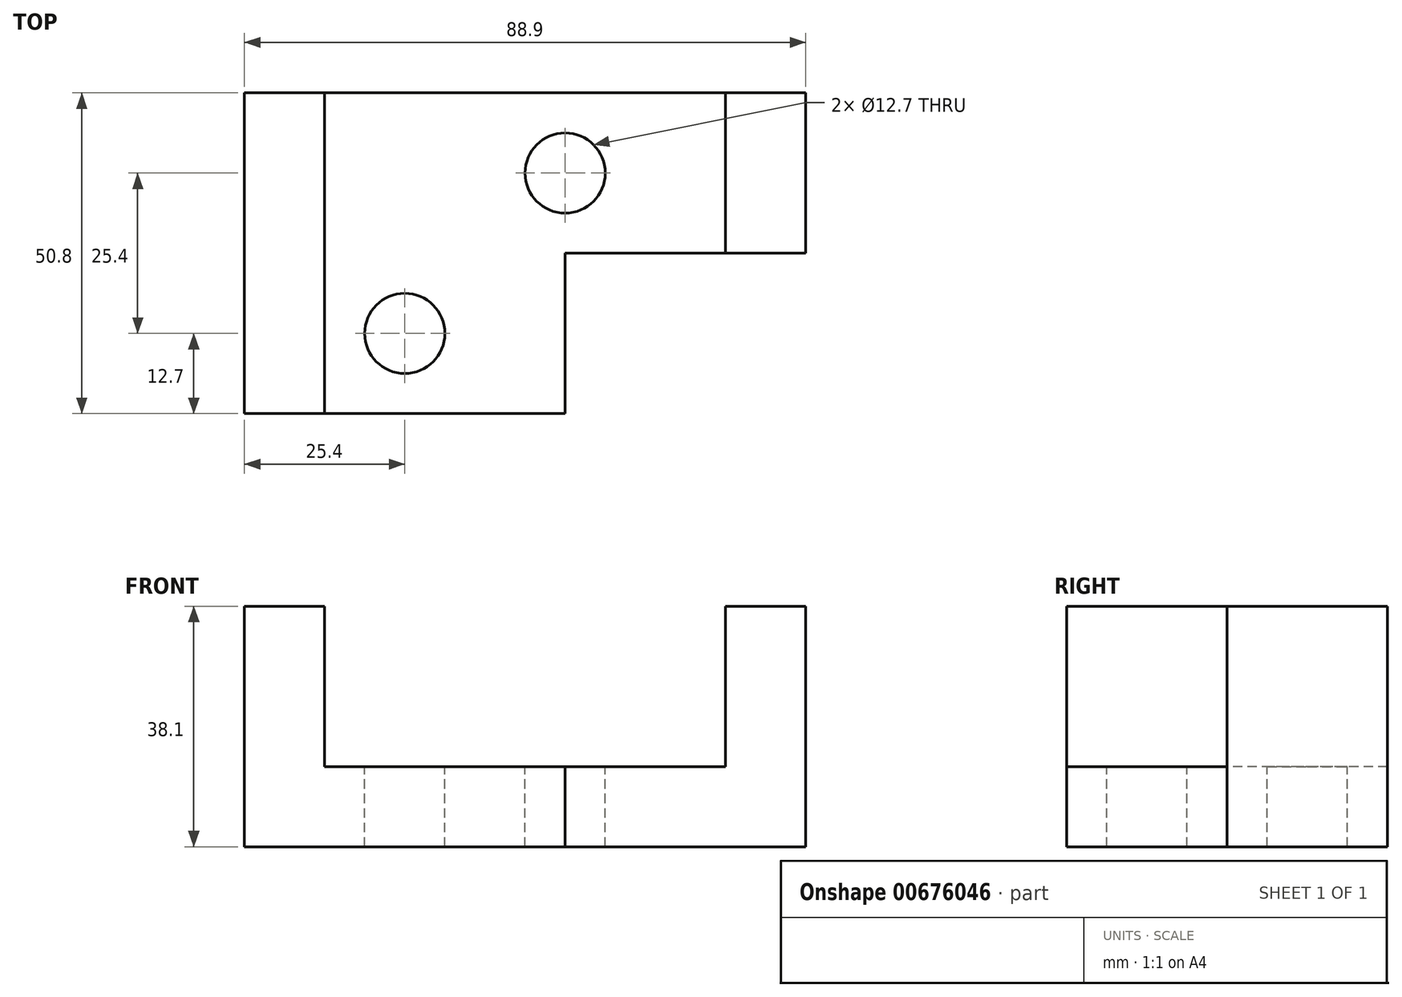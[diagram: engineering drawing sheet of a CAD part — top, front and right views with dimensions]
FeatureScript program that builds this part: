
annotation { "Feature Type Name" : "Feature", "Feature Type Description" : "" }
export const myFeature = defineFeature(function(context is Context, id is Id, definition is map)
    precondition{}
    {
        {
            var Q0;
            Q0=qCreatedBy(makeId("Front.planeOp"),FACE);
            var sketch = newSketch(context, id + "F0", { "sketchPlane" : qUnion([Q0])});
            skLineSegment(sketch, "E0.bottom", {"start": v(-44.45, 19.05) * mm, "end": v(44.45, 19.05) * mm});
            skLineSegment(sketch, "E0.top", {"start": v(-44.45, -19.05) * mm, "end": v(44.45, -19.05) * mm});
            skLineSegment(sketch, "E0.left", {"start": v(-44.45, 19.05) * mm, "end": v(-44.45, -19.05) * mm});
            skLineSegment(sketch, "E0.right", {"start": v(44.45, 19.05) * mm, "end": v(44.45, -19.05) * mm});
            skPoint(sketch, "E0.middle", {"position": v(0, 0) * mm});
            skPoint(sketch, "E1.middle", {"position": v(0, 19.05) * mm});
            skSolve(sketch);
        }
        {
            var Q0;
            Q0 = qSketchRegion(id + "F0", true);
            extrude(context, id + "F1", {"entities" : qUnion([Q0]), "depth" : 50.8 * mm, "offsetDistance" : 25.4 * mm});
        }
        {
            var Q0;
            Q0=makeQuery(id+"F1.opExtrude","CAP_FACE",FACE,{"disambiguationData":[OSD([sQuery(id+"F0.wireOp",EDGE,"E0.bottom"),sQuery(id+"F0.wireOp",EDGE,"E0.top"),sQuery(id+"F0.wireOp",EDGE,"E0.left"),sQuery(id+"F0.wireOp",EDGE,"E0.right")])],"isStart":false});
            var sketch = newSketch(context, id + "F2", { "sketchPlane" : qUnion([Q0])});
            skLineSegment(sketch, "E2.bottom", {"start": v(-31.75, 19.05) * mm, "end": v(31.75, 19.05) * mm});
            skLineSegment(sketch, "E2.top", {"start": v(-31.75, -6.35) * mm, "end": v(31.75, -6.35) * mm});
            skLineSegment(sketch, "E2.left", {"start": v(-31.75, 19.05) * mm, "end": v(-31.75, -6.35) * mm});
            skLineSegment(sketch, "E2.right", {"start": v(31.75, 19.05) * mm, "end": v(31.75, -6.35) * mm});
            skPoint(sketch, "E2.middle", {"position": v(0, 6.35) * mm});
            skSolve(sketch);
        }
        {
            var Q0;
            Q0 = qSketchRegion(id + "F2", true);
            extrude(context, id + "F3", {"entities" : qUnion([Q0]), "operationType" : NewBodyOperationType.REMOVE, "endBound" : BoundingType.THROUGH_ALL, "oppositeDirection" : true, "depth" : 25.4 * mm, "offsetDistance" : 25.4 * mm});
        }
        {
            var Q0;
            {var subQ0=sQuery(id+"F0.wireOp",EDGE,"E0.right");var subQ3=sQuery(id+"F0.wireOp",EDGE,"E0.bottom");Q0=makeQuery(id+"F3.boolean.opBoolean","SPLIT",FACE,{"disambiguationData":[TD([makeQuery(id+"F1.opExtrude","SWEPT_FACE",FACE,{"disambiguationData":[OSD([subQ0])]})])],"derivedFrom":makeQuery(id+"F1.opExtrude","SWEPT_FACE",FACE,{"disambiguationData":[OSD([subQ3])]})});}
            var sketch = newSketch(context, id + "F4", { "sketchPlane" : qUnion([Q0])});
            skLineSegment(sketch, "E3.bottom", {"start": v(44.45, -50.8) * mm, "end": v(6.35, -50.8) * mm});
            skLineSegment(sketch, "E3.top", {"start": v(44.45, -25.4) * mm, "end": v(6.35, -25.4) * mm});
            skLineSegment(sketch, "E3.left", {"start": v(44.45, -50.8) * mm, "end": v(44.45, -25.4) * mm});
            skLineSegment(sketch, "E3.right", {"start": v(6.35, -50.8) * mm, "end": v(6.35, -25.4) * mm});
            skSolve(sketch);
        }
        {
            var Q0;
            Q0 = qSketchRegion(id + "F4", true);
            extrude(context, id + "F5", {"entities" : qUnion([Q0]), "operationType" : NewBodyOperationType.REMOVE, "endBound" : BoundingType.THROUGH_ALL, "oppositeDirection" : true, "depth" : 25.4 * mm, "offsetDistance" : 25.4 * mm});
        }
        {
            var Q0;
            Q0=makeQuery(id+"F3.boolean.opBoolean","COPY",FACE,{"derivedFrom":makeQuery(id+"F3.opExtrude","SWEPT_FACE",FACE,{"disambiguationData":[OSD([sQuery(id+"F2.wireOp",EDGE,"E2.top")])]})});
            var sketch = newSketch(context, id + "F6", { "sketchPlane" : qUnion([Q0])});
            skCircle(sketch, "E4", {"center": v(-19.05, -38.1) * mm, "radius": 6.35 * mm});
            skSolve(sketch);
        }
        {
            var Q0;
            Q0 = qSketchRegion(id + "F6", true);
            extrude(context, id + "F7", {"entities" : qUnion([Q0]), "operationType" : NewBodyOperationType.REMOVE, "endBound" : BoundingType.THROUGH_ALL, "oppositeDirection" : true, "depth" : 25.4 * mm, "offsetDistance" : 25.4 * mm});
        }
        {
            var Q0;
            Q0=makeQuery(id+"F3.boolean.opBoolean","COPY",FACE,{"derivedFrom":makeQuery(id+"F3.opExtrude","SWEPT_FACE",FACE,{"disambiguationData":[OSD([sQuery(id+"F2.wireOp",EDGE,"E2.top")])]})});
            var sketch = newSketch(context, id + "F8", { "sketchPlane" : qUnion([Q0])});
            skCircle(sketch, "E5", {"center": v(6.35, -12.7) * mm, "radius": 6.35 * mm});
            skSolve(sketch);
        }
        {
            var Q0;
            Q0 = qSketchRegion(id + "F8", true);
            extrude(context, id + "F9", {"entities" : qUnion([Q0]), "operationType" : NewBodyOperationType.REMOVE, "endBound" : BoundingType.THROUGH_ALL, "oppositeDirection" : true, "depth" : 25.4 * mm, "offsetDistance" : 25.4 * mm});
        }
    });
